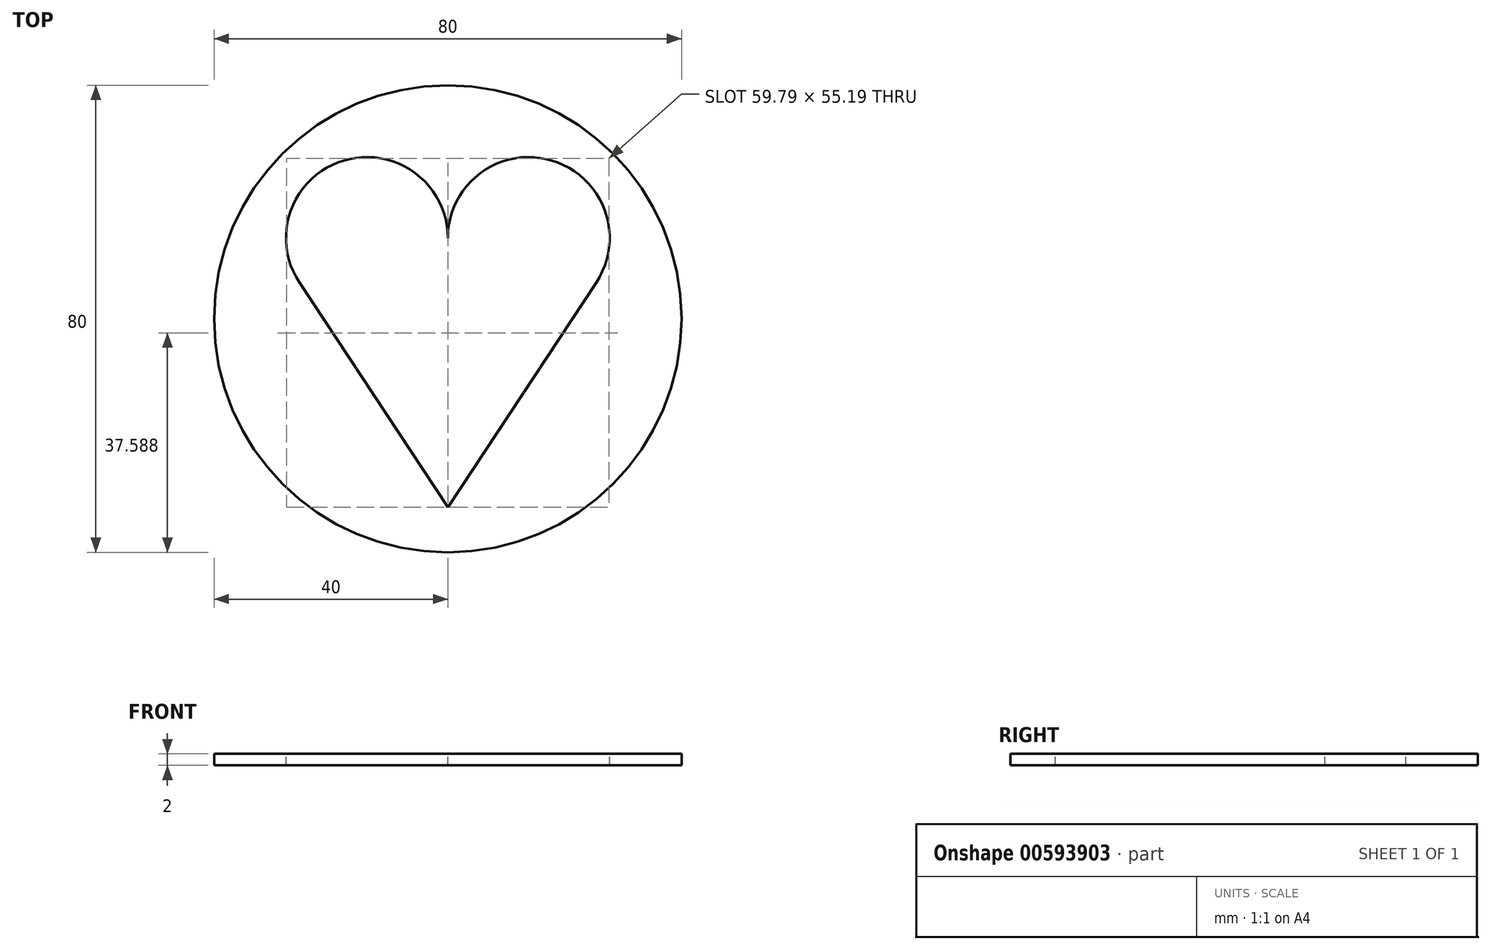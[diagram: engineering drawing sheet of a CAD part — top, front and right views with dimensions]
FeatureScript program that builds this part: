
annotation { "Feature Type Name" : "Feature", "Feature Type Description" : "" }
export const myFeature = defineFeature(function(context is Context, id is Id, definition is map)
    precondition{}
    {
        {
            var Q0;
            Q0=qCreatedBy(makeId("Top.planeOp"),FACE);
            var sketch = newSketch(context, id + "F0", { "sketchPlane" : qUnion([Q0])});
            skCircle(sketch, "E0", {"center": v(0, 0) * mm, "radius": 40 * mm});
            skSolve(sketch);
        }
        {
            var Q0;
            Q0 = qSketchRegion(id + "F0", true);
            extrude(context, id + "F1", {"entities" : qUnion([Q0]), "depth" : 2 * mm, "offsetDistance" : 25 * mm});
        }
        {
            var Q0;
            Q0=makeQuery(id+"F1.opExtrude","CAP_FACE",FACE,{"disambiguationData":[OSD([sQuery(id+"F0.wireOp",EDGE,"E0")])],"isStart":false});
            var sketch = newSketch(context, id + "F2", { "sketchPlane" : qUnion([Q0])});
            skLineSegment(sketch, "E1", {"start": v(0, 13.85) * mm, "end": v(-13.85, 13.85) * mm, "construction": true});
            skLineSegment(sketch, "E2", {"start": v(0, 13.85) * mm, "end": v(0, 0) * mm, "construction": true});
            skCircle(sketch, "E3", {"center": v(-13.85, 13.85) * mm, "radius": 13.85 * mm});
            skLineSegment(sketch, "E4", {"start": v(0, 13.85) * mm, "end": v(0, -32.3) * mm, "construction": true});
            skPoint(sketch, "E5", {"position": v(0, -32.3) * mm});
            skLineSegment(sketch, "E6", {"start": v(-25.4, 6.22) * mm, "end": v(0, -32.3) * mm});
            skCircle(sketch, "E7.MirrorC", {"center": v(13.85, 13.85) * mm, "radius": 13.85 * mm});
            skLineSegment(sketch, "E8.MirrorCS", {"start": v(25.4, 6.22) * mm, "end": v(0, -32.3) * mm});
            skLineSegment(sketch, "E9", {"start": v(-13.85, 27.7) * mm, "end": v(13.85, 27.7) * mm, "construction": true});
            skSolve(sketch);
        }
        {
            var Q0;
            Q0 = qSketchRegion(id + "F2", true);
            extrude(context, id + "F3", {"entities" : qUnion([Q0]), "operationType" : NewBodyOperationType.REMOVE, "oppositeDirection" : true, "depth" : 25 * mm, "offsetDistance" : 25 * mm});
        }
    });
